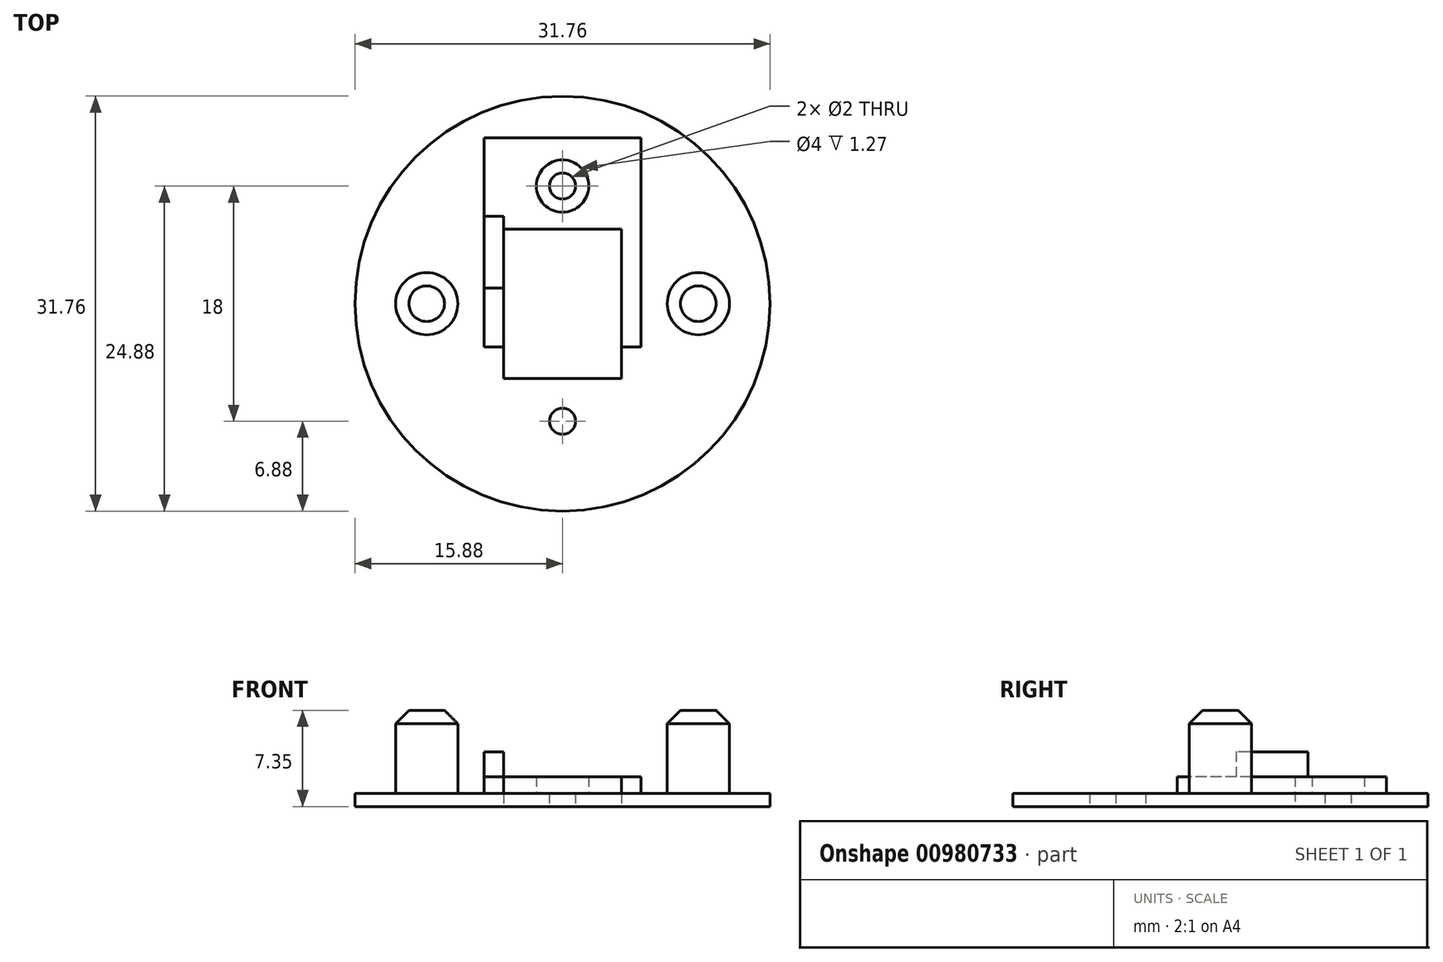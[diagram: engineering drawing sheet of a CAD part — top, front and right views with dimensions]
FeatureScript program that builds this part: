
annotation { "Feature Type Name" : "Feature", "Feature Type Description" : "" }
export const myFeature = defineFeature(function(context is Context, id is Id, definition is map)
    precondition{}
    {
        {
            var Q0;
            Q0=qCreatedBy(makeId("Top.planeOp"),FACE);
            var sketch = newSketch(context, id + "F0", { "sketchPlane" : qUnion([Q0])});
            skCircle(sketch, "E0", {"center": v(0, 0) * mm, "radius": 15.88 * mm});
            skLineSegment(sketch, "E1.bottom", {"start": v(4.5, 5.72) * mm, "end": v(-4.5, 5.72) * mm});
            skLineSegment(sketch, "E1.top", {"start": v(4.5, -5.72) * mm, "end": v(-4.5, -5.72) * mm});
            skLineSegment(sketch, "E1.left", {"start": v(4.5, 5.72) * mm, "end": v(4.5, -5.72) * mm});
            skLineSegment(sketch, "E1.right", {"start": v(-4.5, 5.72) * mm, "end": v(-4.5, -5.72) * mm});
            skCircle(sketch, "E2", {"center": v(0, 9) * mm, "radius": 1 * mm});
            skCircle(sketch, "E3", {"center": v(0, -9) * mm, "radius": 1 * mm});
            skLineSegment(sketch, "E4", {"start": v(0, 9) * mm, "end": v(0, -9) * mm, "construction": true});
            skSolve(sketch);
        }
        {
            var Q0;
            Q0 = qSketchRegion(id + "F0", true);
            extrude(context, id + "F1", {"entities" : qUnion([Q0]), "depth" : 1 * mm, "offsetDistance" : 25.4 * mm});
        }
        {
            var Q0;
            Q0=makeQuery(id+"F1.opExtrude","CAP_FACE",FACE,{"disambiguationData":[OSD([sQuery(id+"F0.wireOp",EDGE,"E0"),sQuery(id+"F0.wireOp",EDGE,"E1.bottom"),sQuery(id+"F0.wireOp",EDGE,"E1.top"),sQuery(id+"F0.wireOp",EDGE,"E1.left"),sQuery(id+"F0.wireOp",EDGE,"E1.right"),sQuery(id+"F0.wireOp",EDGE,"E2"),sQuery(id+"F0.wireOp",EDGE,"E3")])],"isStart":false});
            var sketch = newSketch(context, id + "F2", { "sketchPlane" : qUnion([Q0])});
            skCircle(sketch, "E5", {"center": v(0, 9) * mm, "radius": 2 * mm});
            skLineSegment(sketch, "E6.bottom", {"start": v(-6, 12.7) * mm, "end": v(6, 12.7) * mm});
            skLineSegment(sketch, "E6.top", {"start": v(-6, -3.3) * mm, "end": v(6, -3.3) * mm, "construction": true});
            skLineSegment(sketch, "E6.left", {"start": v(-6, 12.7) * mm, "end": v(-6, -3.3) * mm});
            skLineSegment(sketch, "E6.right", {"start": v(6, 12.7) * mm, "end": v(6, -3.3) * mm});
            skPoint(sketch, "E6.middle", {"position": v(0, 4.7) * mm});
            skLineSegment(sketch, "E7", {"start": v(-6, -3.3) * mm, "end": v(-4.5, -3.3) * mm});
            skLineSegment(sketch, "E8", {"start": v(-4.5, -3.3) * mm, "end": v(-4.5, 5.72) * mm});
            skLineSegment(sketch, "E9", {"start": v(-4.5, 5.72) * mm, "end": v(4.5, 5.72) * mm});
            skLineSegment(sketch, "E10", {"start": v(4.5, 5.72) * mm, "end": v(4.5, -3.3) * mm});
            skLineSegment(sketch, "E11", {"start": v(4.5, -3.3) * mm, "end": v(6, -3.3) * mm});
            skPoint(sketch, "E12", {"position": v(-6, 14.7) * mm});
            skSolve(sketch);
        }
        {
            var Q0;
            Q0 = qSketchRegion(id + "F2", true);
            extrude(context, id + "F3", {"entities" : qUnion([Q0]), "operationType" : NewBodyOperationType.ADD, "depth" : 1.27 * mm, "offsetDistance" : 25.4 * mm});
        }
        {
            var Q0;
            Q0=makeQuery(id+"F3.opExtrude","CAP_FACE",FACE,{"disambiguationData":[OSD([sQuery(id+"F2.wireOp",EDGE,"E5"),sQuery(id+"F2.wireOp",EDGE,"E6.bottom"),sQuery(id+"F2.wireOp",EDGE,"E6.left"),sQuery(id+"F2.wireOp",EDGE,"E6.right"),sQuery(id+"F2.wireOp",EDGE,"E7"),sQuery(id+"F2.wireOp",EDGE,"E8"),sQuery(id+"F2.wireOp",EDGE,"E9"),sQuery(id+"F2.wireOp",EDGE,"E10"),sQuery(id+"F2.wireOp",EDGE,"E11")])],"isStart":false});
            var sketch = newSketch(context, id + "F4", { "sketchPlane" : qUnion([Q0])});
            skLineSegment(sketch, "E13.bottom", {"start": v(-6, 6.7) * mm, "end": v(-4.5, 6.7) * mm});
            skLineSegment(sketch, "E13.top", {"start": v(-6, 1.2) * mm, "end": v(-4.5, 1.2) * mm});
            skLineSegment(sketch, "E13.left", {"start": v(-6, 6.7) * mm, "end": v(-6, 1.2) * mm});
            skLineSegment(sketch, "E13.right", {"start": v(-4.5, 6.7) * mm, "end": v(-4.5, 1.2) * mm});
            skSolve(sketch);
        }
        {
            var Q0;
            Q0 = qSketchRegion(id + "F4", true);
            extrude(context, id + "F5", {"entities" : qUnion([Q0]), "operationType" : NewBodyOperationType.ADD, "depth" : 1.9 * mm, "offsetDistance" : 25.4 * mm});
        }
        {
            var Q0;
            {var subQ0=sQuery(id+"F0.wireOp",EDGE,"E3");var subQ1=sQuery(id+"F0.wireOp",EDGE,"E0");var subQ2=sQuery(id+"F0.wireOp",EDGE,"E1.left");var subQ3=sQuery(id+"F0.wireOp",EDGE,"E1.top");var subQ4=sQuery(id+"F0.wireOp",EDGE,"E1.right");Q0=makeQuery(id+"F3.boolean.opBoolean","SPLIT",FACE,{"disambiguationData":[TD([makeQuery(id+"F1.opExtrude","SWEPT_FACE",FACE,{"disambiguationData":[OSD([subQ1])]})])],"derivedFrom":makeQuery(id+"F1.opExtrude","CAP_FACE",FACE,{"disambiguationData":[OSD([subQ1,sQuery(id+"F0.wireOp",EDGE,"E1.bottom"),subQ3,subQ2,subQ4,sQuery(id+"F0.wireOp",EDGE,"E2"),subQ0])],"isStart":false})});}
            var sketch = newSketch(context, id + "F6", { "sketchPlane" : qUnion([Q0])});
            skCircle(sketch, "E14", {"center": v(10.39, 0) * mm, "radius": 2.38 * mm});
            skCircle(sketch, "E15", {"center": v(-10.39, 0) * mm, "radius": 2.38 * mm});
            skLineSegment(sketch, "E16", {"start": v(-10.39, 0) * mm, "end": v(10.39, 0) * mm, "construction": true});
            skSolve(sketch);
        }
        {
            var Q0;
            Q0 = qSketchRegion(id + "F6", true);
            var Q1;
            Q1=makeQuery(id+"FjvVrHLhEV2LxPh_1.opExtrude","CAP_FACE",FACE,{"disambiguationData":[OSD([sQuery(id+"Fhgg7KqzgV7qigf_1.wireOp",EDGE,"6oGU95zO-utdY-0rm4-JIIB-4pLrA47s5ZBC"),sQuery(id+"Fhgg7KqzgV7qigf_1.wireOp",EDGE,"wU8sd21L-gYQr-tsDK-jVAz-xp2IdvGSuyiG")])],"isStart":false});
            extrude(context, id + "F7", {"entities" : qUnion([Q0]), "operationType" : NewBodyOperationType.ADD, "depth" : 6.35 * mm, "endBoundEntityFace" : qUnion([Q1]), "hasOffset" : true, "offsetDistance" : 3.8 * mm, "offsetOppositeDirection" : true});
        }
        {
            var Q0;
            Q0=makeQuery(id+"F7.opExtrude","CAP_FACE",FACE,{"disambiguationData":[OSD([sQuery(id+"F6.wireOp",EDGE,"E15")])],"isStart":false});
            var Q1;
            Q1=makeQuery(id+"F7.opExtrude","CAP_FACE",FACE,{"disambiguationData":[OSD([sQuery(id+"F6.wireOp",EDGE,"E14")])],"isStart":false});
            chamfer(context, id + "F8", {"entities" : qUnion([Q0, Q1]), "width" : 1.02 * mm, "tangentPropagation" : true});
        }
    });
